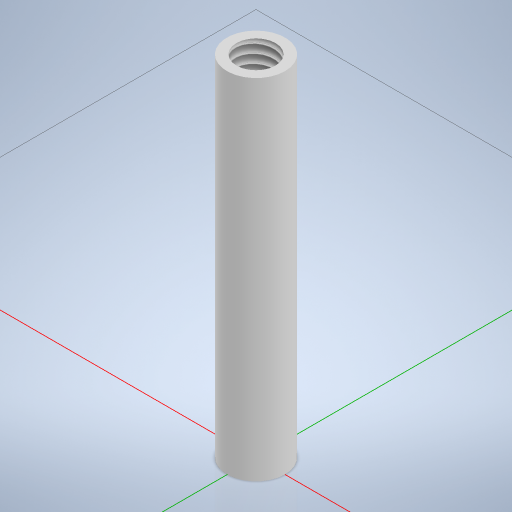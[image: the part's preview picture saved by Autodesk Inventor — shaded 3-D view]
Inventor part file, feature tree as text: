
AUTODESK INVENTOR PART (.ipt)
format: ipt  version: 2024 (Build 280153000, 153)  size: 238,592 bytes
history: native  units: mm
features: sketch x2, extrude x1, hole x1
ambient origin geometry x8: Origin, YZ Plane, XZ Plane, XY Plane, X Axis, Y Axis, Z Axis, Center Point
bodies: Volumenkörper1 (feature_tree)
feature tree (4):
  extrude  "Extrusion1"  Depth=18.0mm TaperAngle=0.0deg
  hole  "Bohrung1"  [1 undecoded]
  sketch  "Skizze1"  dims[d0=3.0mm d1=18.0mm d2=0.0mm]
  sketch  "Skizze2"  dims[d3=2.013mm d4=5.0mm d5=10.0mm d6=4.0mm d7=90.0deg d8=9.5mm d9=0.0mm]
note: 1 required parameter value undecoded (feature->parameter linkage not recoverable at this tier; creation-order binding heuristic only, values carry confidence <= 0.55)
